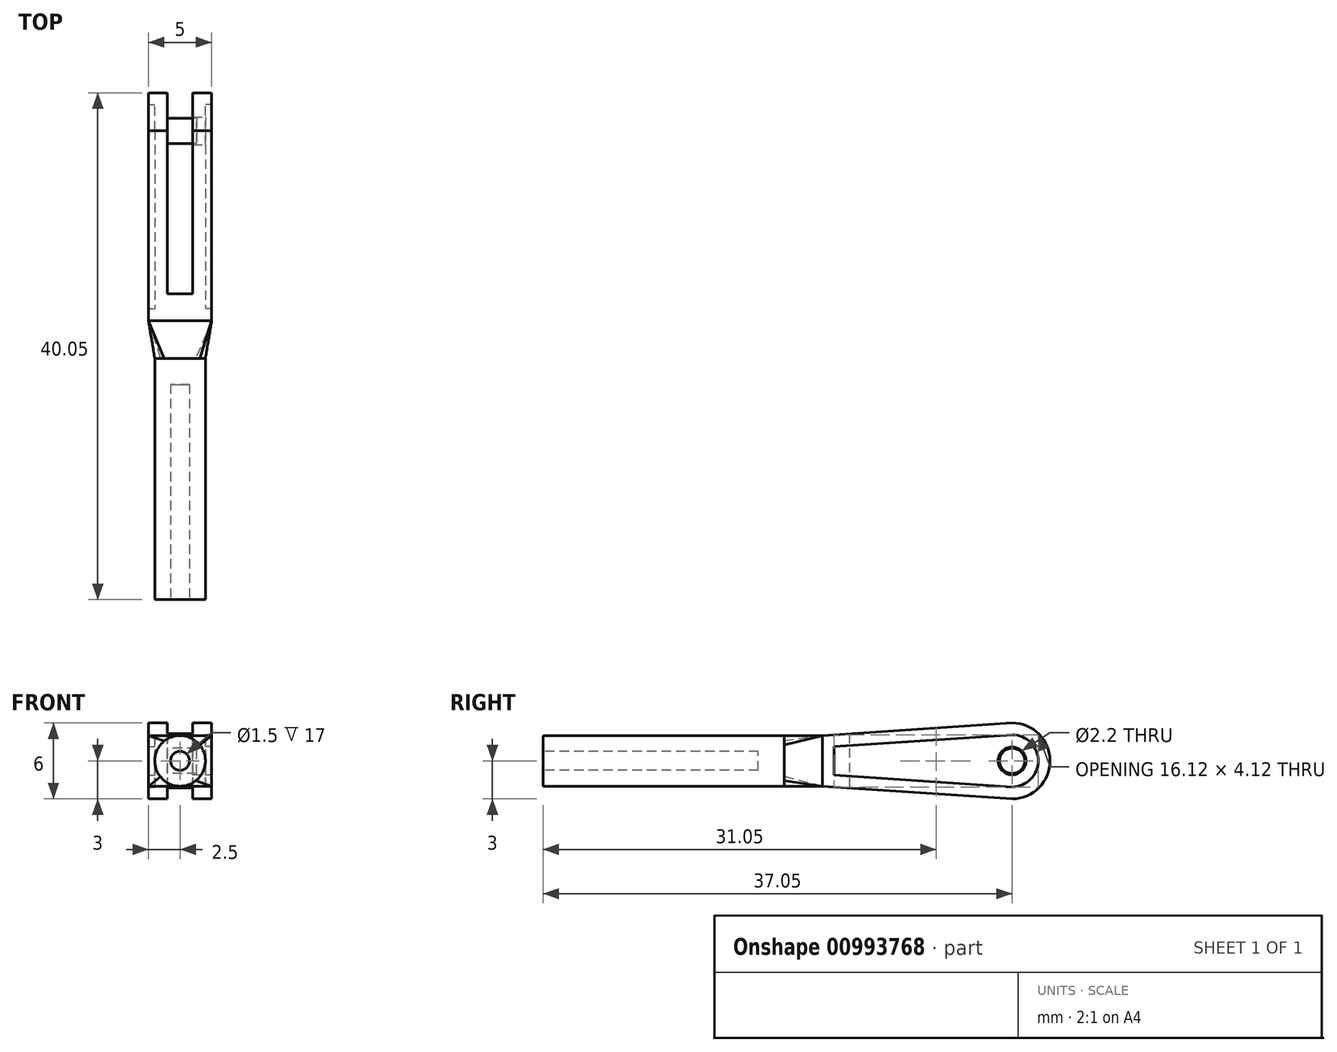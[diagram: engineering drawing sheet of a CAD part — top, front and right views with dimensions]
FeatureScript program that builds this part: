
annotation { "Feature Type Name" : "Feature", "Feature Type Description" : "" }
export const myFeature = defineFeature(function(context is Context, id is Id, definition is map)
    precondition{}
    {
        {
            var Q0;
            Q0=qCreatedBy(makeId("Front.planeOp"),FACE);
            var sketch = newSketch(context, id + "F0", { "sketchPlane" : qUnion([Q0])});
            skCircle(sketch, "E0", {"center": v(0, 0) * mm, "radius": 2 * mm});
            skCircle(sketch, "E1", {"center": v(0, 0) * mm, "radius": 0.75 * mm});
            skSolve(sketch);
        }
        {
            var Q0;
            Q0=makeQuery(id+"F0.imprint","IMPRINT",FACE,{"disambiguationData":[TD([[makeQuery(id+"F0.imprint","IMPRINT",EDGE,{"derivedFrom":sQuery(id+"F0.wireOp",EDGE,"E0")}),1.0]])]});
            var Q1;
            Q1=makeQuery(id+"F0.imprint","IMPRINT",FACE,{"disambiguationData":[TD([[makeQuery(id+"F0.imprint","IMPRINT",EDGE,{"derivedFrom":sQuery(id+"F0.wireOp",EDGE,"E1")}),1.0]])]});
            extrude(context, id + "F1", {"entities" : qUnion([Q0, Q1]), "depth" : 19.05 * mm, "offsetDistance" : 25.4 * mm});
        }
        {
            var Q0;
            Q0=qCreatedBy(makeId("Right.planeOp"),FACE);
            var sketch = newSketch(context, id + "F2", { "sketchPlane" : qUnion([Q0])});
            skLineSegment(sketch, "E2.0", {"start": v(3, -2) * mm, "end": v(3, 2) * mm});
            skCircle(sketch, "E3", {"center": v(18, 0) * mm, "radius": 3 * mm});
            skLineSegment(sketch, "E4", {"start": v(18, -3) * mm, "end": v(18, 3) * mm, "construction": true});
            skLineSegment(sketch, "E5", {"start": v(18, 3) * mm, "end": v(3, 2) * mm});
            skLineSegment(sketch, "E6", {"start": v(18, -3) * mm, "end": v(3, -2) * mm});
            skCircle(sketch, "E7", {"center": v(18, 0) * mm, "radius": 1 * mm});
            skSolve(sketch);
        }
        {
            var Q0;
            Q0=makeQuery(id+"F2.imprint","IMPRINT",FACE,{"disambiguationData":[TD([[makeQuery(id+"F2.imprint","IMPRINT",EDGE,{"derivedFrom":sQuery(id+"F2.wireOp",EDGE,"waPN0C9D-aEQh-yq3H-stLx-nCHPpKASFijS")}),1.0]])]});
            var Q1;
            {var subQ0=sQuery(id+"F2.wireOp",EDGE,"E2.0");Q1=makeQuery(id+"F2.imprint","IMPRINT",FACE,{"disambiguationData":[TD([[makeQuery(id+"F2.imprint","IMPRINT",EDGE,{"derivedFrom":subQ0}),-1.0]])]});}
            var Q2;
            Q2=makeQuery(id+"F2.imprint","IMPRINT",FACE,{"disambiguationData":[TD([[makeQuery(id+"F2.imprint","IMPRINT",EDGE,{"derivedFrom":sQuery(id+"F2.wireOp",EDGE,"E7")}),-1.0]])]});
            var Q3;
            Q3=makeQuery(id+"F2.imprint","IMPRINT",FACE,{"disambiguationData":[TD([[makeQuery(id+"F2.imprint","IMPRINT",EDGE,{"derivedFrom":sQuery(id+"F2.wireOp",EDGE,"E7")}),1.0]])]});
            extrude(context, id + "F3", {"entities" : qUnion([Q0, Q1, Q2, Q3]), "endBound" : BoundingType.SYMMETRIC, "depth" : 4 * mm, "offsetDistance" : 25.4 * mm});
        }
        {
            var Q0;
            Q0=qCreatedBy(makeId("Top.planeOp"),FACE);
            var sketch = newSketch(context, id + "F4", { "sketchPlane" : qUnion([Q0])});
            skLineSegment(sketch, "E8.bottom", {"start": v(1, 26.49) * mm, "end": v(-1, 26.49) * mm});
            skLineSegment(sketch, "E8.top", {"start": v(1, 5.13) * mm, "end": v(-1, 5.13) * mm});
            skLineSegment(sketch, "E8.left", {"start": v(1, 26.49) * mm, "end": v(1, 5.13) * mm});
            skLineSegment(sketch, "E8.right", {"start": v(-1, 26.49) * mm, "end": v(-1, 5.13) * mm});
            skPoint(sketch, "E8.middle", {"position": v(0, 15.8) * mm});
            skSolve(sketch);
        }
        {
            var Q0;
            Q0=makeQuery(id+"F4.imprint","IMPRINT",FACE,{"disambiguationData":[TD([[makeQuery(id+"F4.imprint","IMPRINT",EDGE,{"derivedFrom":sQuery(id+"F4.wireOp",EDGE,"E8.bottom")}),1.0]])]});
            extrude(context, id + "F5", {"entities" : qUnion([Q0]), "endBound" : BoundingType.SYMMETRIC, "depth" : 25 * mm, "offsetDistance" : 25 * mm});
        }
        {
            var Q0;
            Q0=makeQuery(id+"F5.opExtrude","SWEPT_BODY",BODY,{"disambiguationData":[OSD([sQuery(id+"F4.wireOp",EDGE,"E8.bottom"),sQuery(id+"F4.wireOp",EDGE,"E8.top"),sQuery(id+"F4.wireOp",EDGE,"E8.left"),sQuery(id+"F4.wireOp",EDGE,"E8.right")])]});
            var Q1;
            Q1=makeQuery(id+"F3.opExtrude","SWEPT_BODY",BODY,{"disambiguationData":[OSD([sQuery(id+"F2.wireOp",EDGE,"E2.0"),sQuery(id+"F2.wireOp",EDGE,"E3"),sQuery(id+"F2.wireOp",EDGE,"E5"),sQuery(id+"F2.wireOp",EDGE,"E6"),sQuery(id+"F2.wireOp",EDGE,"E7")])]});
            booleanBodies(context, id + "F6", {"operationType" : BooleanOperationType.SUBTRACTION, "tools" : qUnion([Q0]), "targets" : qUnion([Q1])});
        }
        {
            var Q0;
            Q0=makeQuery(id+"F1.opExtrude","CAP_FACE",FACE,{"disambiguationData":[OSD([sQuery(id+"F0.wireOp",EDGE,"E0")])],"isStart":false});
            var sketch = newSketch(context, id + "F7", { "sketchPlane" : qUnion([Q0])});
            skCircle(sketch, "E9", {"center": v(0, 0) * mm, "radius": 0.75 * mm});
            skSolve(sketch);
        }
        {
            var Q0;
            Q0=qSketchRegion(id+"F7",true);
            extrude(context, id + "F8", {"entities" : qUnion([Q0]), "operationType" : NewBodyOperationType.REMOVE, "oppositeDirection" : true, "depth" : 17 * mm, "offsetDistance" : 25 * mm});
        }
        {
            var Q0;
            Q0=makeQuery(id+"F3.opExtrude","CAP_FACE",FACE,{"disambiguationData":[OSD([sQuery(id+"F2.wireOp",EDGE,"E2.0"),sQuery(id+"F2.wireOp",EDGE,"E3"),sQuery(id+"F2.wireOp",EDGE,"E5"),sQuery(id+"F2.wireOp",EDGE,"E6"),sQuery(id+"F2.wireOp",EDGE,"E7")])],"isStart":true});
            var sketch = newSketch(context, id + "F9", { "sketchPlane" : qUnion([Q0])});
            skLineSegment(sketch, "E10.0", {"start": v(-18.03, -2.06) * mm, "end": v(-3.94, -1.12) * mm});
            skArc(sketch, "E10.1", {"start": v(-18.03, 2.06) * mm, "mid": v(-20.06, 0) * mm, "end": v(-18.03, -2.06) * mm});
            skLineSegment(sketch, "E10.2", {"start": v(-3.94, 1.12) * mm, "end": v(-18.03, 2.06) * mm});
            skLineSegment(sketch, "E10.3", {"start": v(-3.94, -1.12) * mm, "end": v(-3.94, 1.12) * mm});
            skLineSegment(sketch, "E11.0", {"start": v(-18, 3) * mm, "end": v(-3, 2) * mm});
            skArc(sketch, "E11.1", {"start": v(-18, -3) * mm, "mid": v(-21, 0) * mm, "end": v(-18, 3) * mm});
            skLineSegment(sketch, "E11.2", {"start": v(-18, -3) * mm, "end": v(-3, -2) * mm});
            skLineSegment(sketch, "E11.3", {"start": v(-3, -2) * mm, "end": v(-3, 2) * mm});
            skSolve(sketch);
        }
        {
            var Q0;
            Q0=qSketchRegion(id+"F9",true);
            var Q1;
            Q1=makeQuery(id+"F9.imprint","IMPRINT",FACE,{"disambiguationData":[TD([[makeQuery(id+"F9.imprint","IMPRINT",EDGE,{"derivedFrom":sQuery(id+"F9.wireOp",EDGE,"E10.0")}),-1.0]])]});
            extrude(context, id + "F10", {"entities" : qUnion([Q0, Q1]), "depth" : .5 * mm, "offsetDistance" : 25 * mm});
        }
        {
            var Q0;
            Q0=makeQuery(id+"F3.opExtrude","CAP_FACE",FACE,{"disambiguationData":[OSD([sQuery(id+"F2.wireOp",EDGE,"E2.0"),sQuery(id+"F2.wireOp",EDGE,"E3"),sQuery(id+"F2.wireOp",EDGE,"E5"),sQuery(id+"F2.wireOp",EDGE,"E6")])],"isStart":false});
            var sketch = newSketch(context, id + "F11", { "sketchPlane" : qUnion([Q0])});
            skPoint(sketch, "E12.0", {"position": v(18, 0) * mm});
            skCircle(sketch, "E13", {"center": v(18, 0) * mm, "radius": 1.1 * mm});
            skSolve(sketch);
        }
        {
            var Q0;
            Q0=makeQuery(id+"F10.opExtrude","SWEPT_BODY",BODY,{"disambiguationData":[OSD([sQuery(id+"F9.wireOp",EDGE,"E10.0"),sQuery(id+"F9.wireOp",EDGE,"E10.1"),sQuery(id+"F9.wireOp",EDGE,"E10.2"),sQuery(id+"F9.wireOp",EDGE,"E10.3"),sQuery(id+"F9.wireOp",EDGE,"E11.0"),sQuery(id+"F9.wireOp",EDGE,"E11.1"),sQuery(id+"F9.wireOp",EDGE,"E11.2"),sQuery(id+"F9.wireOp",EDGE,"E11.3")])]});
            var Q1;
            Q1=qCreatedBy(makeId("Right.planeOp"),FACE);
            mirror(context, id + "F12", {"operationType" : NewBodyOperationType.ADD, "entities" : qUnion([Q0]), "mirrorPlane" : qUnion([Q1])});
        }
        {
            var Q0;
            Q0=makeQuery(id+"F3.opExtrude","SWEPT_FACE",FACE,{"disambiguationData":[OSD([sQuery(id+"F2.wireOp",EDGE,"E2.0")])]});
            var sketch = newSketch(context, id + "F13", { "sketchPlane" : qUnion([Q0])});
            skPoint(sketch, "E14.0", {"position": v(2.5, 2) * mm});
            skPoint(sketch, "E14.1", {"position": v(-2.5, -2) * mm});
            skLineSegment(sketch, "E15.bottom", {"start": v(2.5, 2) * mm, "end": v(-2.5, 2) * mm});
            skLineSegment(sketch, "E15.top", {"start": v(2.5, -2) * mm, "end": v(-2.5, -2) * mm});
            skLineSegment(sketch, "E15.left", {"start": v(2.5, 2) * mm, "end": v(2.5, -2) * mm});
            skLineSegment(sketch, "E15.right", {"start": v(-2.5, 2) * mm, "end": v(-2.5, -2) * mm});
            skSolve(sketch);
        }
        {
            var Q0;
            Q0=makeQuery(id+"F1.opExtrude","CAP_FACE",FACE,{"disambiguationData":[OSD([sQuery(id+"F0.wireOp",EDGE,"E0")])],"isStart":true});
            var sketch = newSketch(context, id + "F14", { "sketchPlane" : qUnion([Q0])});
            skArc(sketch, "E16", {"start": v(-1.55, 1.27) * mm, "mid": v(-2, 0) * mm, "end": v(-1.54, -1.28) * mm});
            skArc(sketch, "E17", {"start": v(-1.54, -1.28) * mm, "mid": v(-0.03, -2) * mm, "end": v(1.5, -1.32) * mm});
            skArc(sketch, "E18", {"start": v(1.5, -1.32) * mm, "mid": v(2, -0.08) * mm, "end": v(1.6, 1.19) * mm});
            skArc(sketch, "E19", {"start": v(1.6, 1.19) * mm, "mid": v(0.05, 2) * mm, "end": v(-1.55, 1.27) * mm});
            skSolve(sketch);
        }
        {
            var Q0;
            Q0=qSketchRegion(id+"F13",true);
            var Q1;
            Q1=makeQuery(id+"F1.opExtrude","CAP_FACE",FACE,{"disambiguationData":[OSD([sQuery(id+"F0.wireOp",EDGE,"E0")])],"isStart":true});
            var Q2;
            Q2=sQuery(id+"F13.wireOp",VERTEX,"E14.1");
            var Q3;
            Q3=sQuery(id+"F14.wireOp",VERTEX,"E17.end");
            var Q4;
            Q4=sQuery(id+"F14.wireOp",VERTEX,"E16.end");
            var Q5;
            Q5=sQuery(id+"F13.wireOp",VERTEX,"E15.top.start");
            loft(context, id + "F15", {"operationType" : NewBodyOperationType.ADD, "sheetProfilesArray" : [{ "sheetProfileEntities" : qUnion([Q0]) }, { "sheetProfileEntities" : qUnion([Q1]) }], "connections" : [{ "connectionEntities" : qUnion([Q2, Q3, Q4, Q5]), "connectionEdgeQueries" : qUnion([]), "connectionEdgeParameters" : [] }]});
        }
        {
            var Q0;
            Q0=makeQuery(id+"F11.imprint","IMPRINT",FACE,{"disambiguationData":[TD([[makeQuery(id+"F11.imprint","IMPRINT",EDGE,{"derivedFrom":sQuery(id+"F11.wireOp",EDGE,"E13")}),1.0]])]});
            var Q1;
            Q1=makeQuery(id+"F6.opBoolean","COPY",FACE,{"derivedFrom":makeQuery(id+"F5.opExtrude","SWEPT_FACE",FACE,{"disambiguationData":[OSD([sQuery(id+"F4.wireOp",EDGE,"E8.left")])]})});
            extrude(context, id + "F16", {"entities" : qUnion([Q0]), "operationType" : NewBodyOperationType.REMOVE, "endBound" : BoundingType.UP_TO_SURFACE, "oppositeDirection" : true, "depth" : 25 * mm, "endBoundEntityFace" : qUnion([Q1]), "offsetDistance" : 25 * mm});
        }
        {
            var Q0;
            Q0=makeQuery(id+"F6.opBoolean","COPY",FACE,{"derivedFrom":makeQuery(id+"F5.opExtrude","SWEPT_FACE",FACE,{"disambiguationData":[OSD([sQuery(id+"F4.wireOp",EDGE,"E8.right")])]})});
            var sketch = newSketch(context, id + "F17", { "sketchPlane" : qUnion([Q0])});
            skCircle(sketch, "E20.0", {"center": v(18, 0) * mm, "radius": 1 * mm});
            skSolve(sketch);
        }
        {
            var Q0;
            Q0=makeQuery(id+"F17.imprint","IMPRINT",FACE,{"disambiguationData":[TD([[makeQuery(id+"F17.imprint","IMPRINT",EDGE,{"derivedFrom":sQuery(id+"F17.wireOp",EDGE,"E20.0")}),1.0]])]});
            var Q1;
            Q1=sQuery(id+"F17.wireOp",EDGE,"E20.0");
            var Q2;
            Q2=makeQuery(id+"F6.opBoolean","COPY",FACE,{"derivedFrom":makeQuery(id+"F5.opExtrude","SWEPT_FACE",FACE,{"disambiguationData":[OSD([sQuery(id+"F4.wireOp",EDGE,"E8.left")])]})});
            extrude(context, id + "F18", {"entities" : qUnion([Q0]), "operationType" : NewBodyOperationType.ADD, "surfaceOperationType" : NewSurfaceOperationType.ADD, "surfaceEntities" : qUnion([Q1]), "depth" : 2.31 * mm, "endBoundEntityFace" : qUnion([Q2]), "offsetDistance" : 25 * mm});
        }
    });
